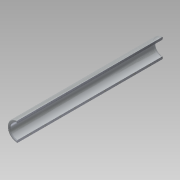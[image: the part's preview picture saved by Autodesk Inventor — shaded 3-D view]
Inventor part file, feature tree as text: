
AUTODESK INVENTOR PART (.ipt)
format: ipt  version: 2014 (Build 180170000, 170)  size: 112,128 bytes
history: native  units: mm
features: fillet x3, other x1, extrude x1, sketch x1
ambient origin geometry x8: Origin, YZ Plane, XZ Plane, XY Plane, X Axis, Y Axis, Z Axis, Center Point
bodies: Body1 (feature_tree)
feature tree (6):
  other  "CrossSection1"
  extrude  "Extrusion2"  Depth=0.3mm
  fillet  "Fillet1"  Radius=60.0mm
  fillet  "Fillet2"  Radius=0.3mm
  fillet  "Fillet3"  Radius=0.3mm
  sketch  "Sketch3"  dims[d4=8.0mm d6=6.0mm d7=60.0mm d8=0.0mm d9=0.3mm d10=0.3mm d11=0.3mm d12=0.5mm d13=2.0mm d14=0.0mm d15=20.0mm]
